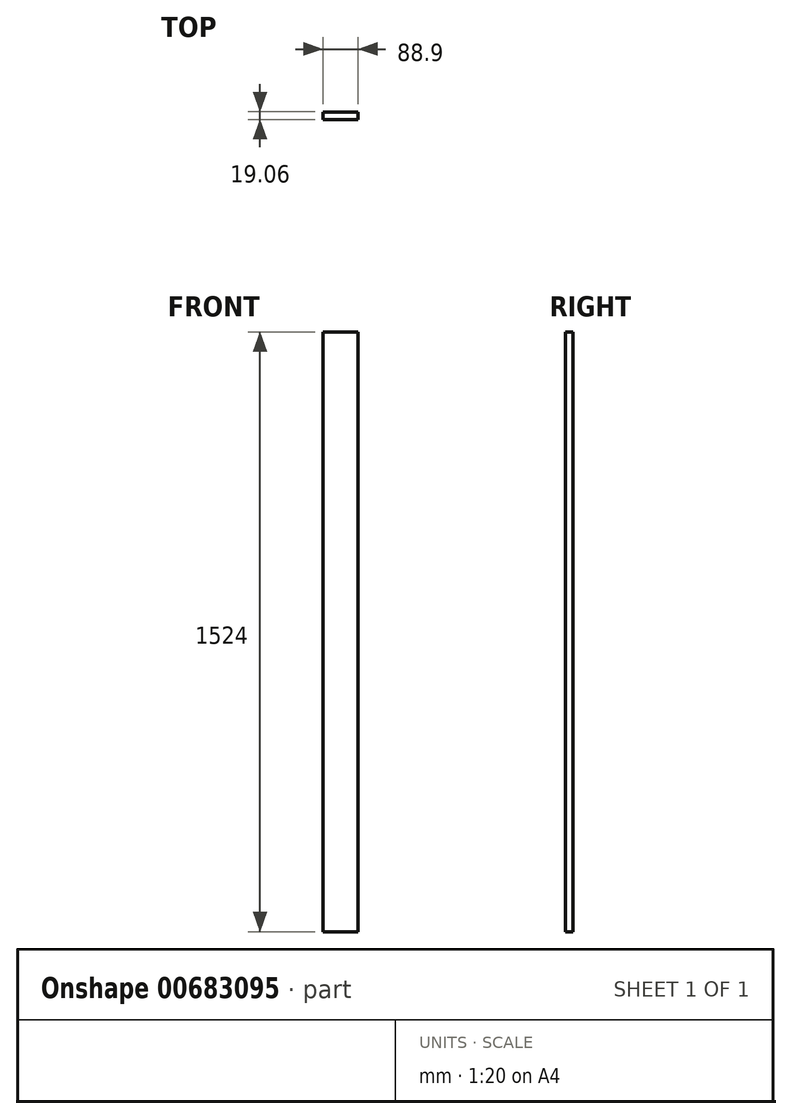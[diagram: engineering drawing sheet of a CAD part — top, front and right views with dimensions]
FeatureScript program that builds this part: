
annotation { "Feature Type Name" : "Feature", "Feature Type Description" : "" }
export const myFeature = defineFeature(function(context is Context, id is Id, definition is map)
    precondition{}
    {
        {
            var Q0;
            Q0=qCreatedBy(makeId("Top.planeOp"),FACE);
            var sketch = newSketch(context, id + "F0", { "sketchPlane" : qUnion([Q0])});
            skLineSegment(sketch, "E0.bottom", {"start": v(44.45, 9.53) * mm, "end": v(-44.45, 9.53) * mm});
            skLineSegment(sketch, "E0.top", {"start": v(44.45, -9.52) * mm, "end": v(-44.45, -9.52) * mm});
            skLineSegment(sketch, "E0.left", {"start": v(44.45, 9.52) * mm, "end": v(44.45, -9.52) * mm});
            skLineSegment(sketch, "E0.right", {"start": v(-44.45, 9.52) * mm, "end": v(-44.45, -9.52) * mm});
            skPoint(sketch, "E0.middle", {"position": v(0, 0) * mm});
            skSolve(sketch);
        }
        {
            var Q0;
            Q0=qSketchRegion(id+"F0",true);
            extrude(context, id + "F1", {"entities" : qUnion([Q0]), "depth" : 1524 * mm, "offsetDistance" : 25.4 * mm});
        }
    });
